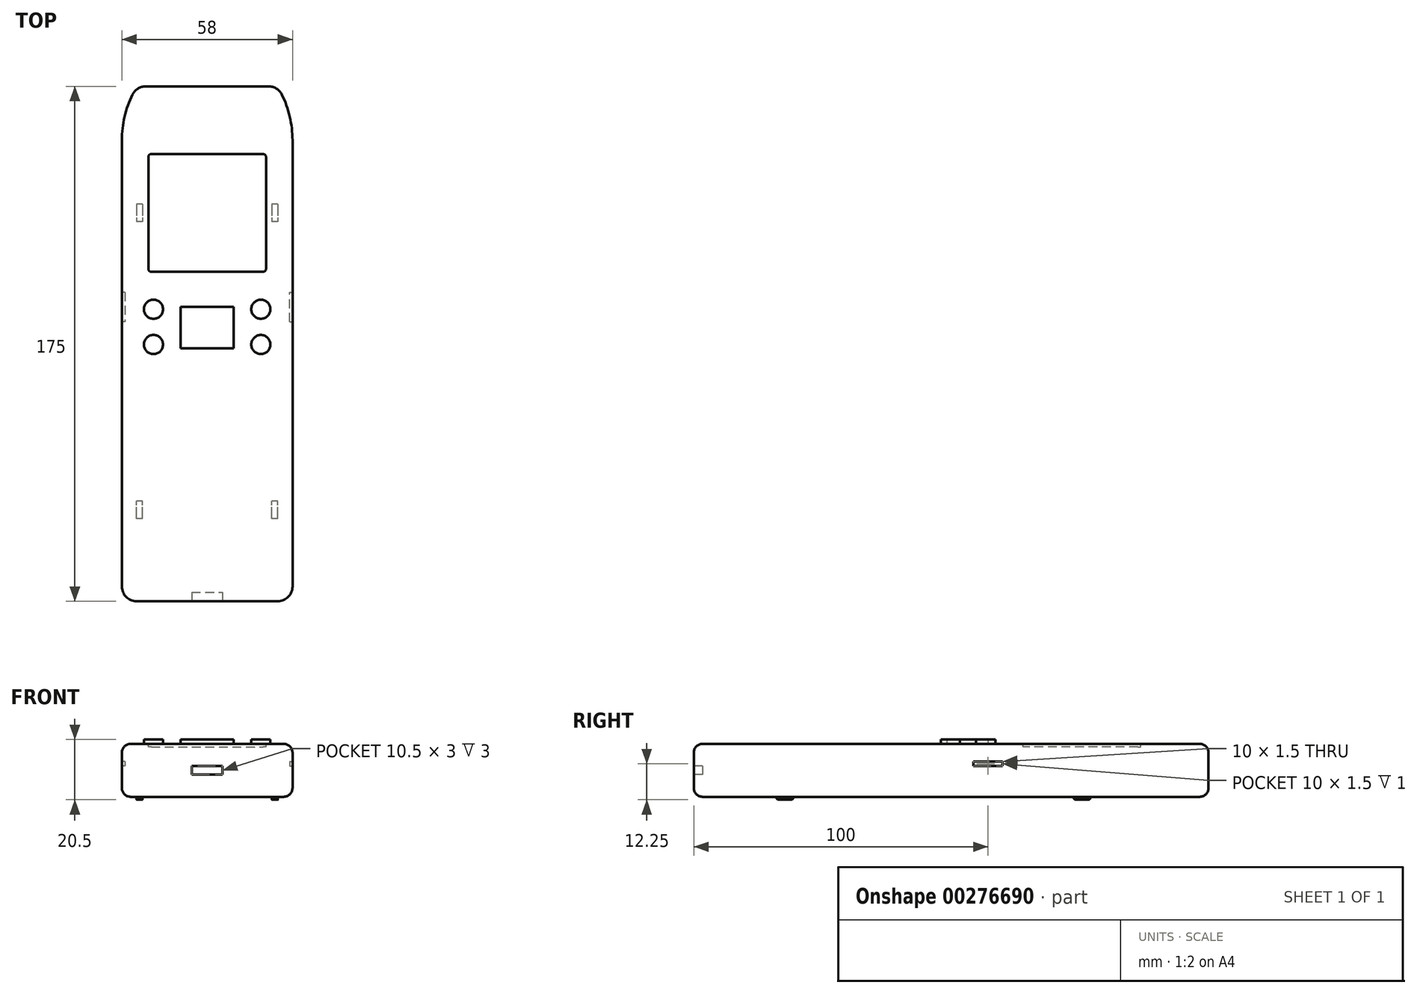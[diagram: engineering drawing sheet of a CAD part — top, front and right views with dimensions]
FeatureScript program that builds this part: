
annotation { "Feature Type Name" : "Feature", "Feature Type Description" : "" }
export const myFeature = defineFeature(function(context is Context, id is Id, definition is map)
    precondition{}
    {
        {
            var Q0;
            Q0=qCreatedBy(makeId("Top.planeOp"),FACE);
            var sketch = newSketch(context, id + "F0", { "sketchPlane" : qUnion([Q0])});
            skLineSegment(sketch, "E0.bottom", {"start": v(0, 0) * mm, "end": v(58, 0) * mm});
            skLineSegment(sketch, "E0.top", {"start": v(0, 175) * mm, "end": v(58, 175) * mm});
            skLineSegment(sketch, "E0.left", {"start": v(0, 0) * mm, "end": v(0, 175) * mm});
            skLineSegment(sketch, "E0.right", {"start": v(58, 0) * mm, "end": v(58, 175) * mm});
            skSolve(sketch);
        }
        {
            var Q0;
            Q0=makeQuery(id+"F0.imprint","IMPRINT",FACE,{"disambiguationData":[TD([[makeQuery(id+"F0.imprint","IMPRINT",EDGE,{"derivedFrom":sQuery(id+"F0.wireOp",EDGE,"E0.bottom")}),1.0]])]});
            extrude(context, id + "F1", {"entities" : qUnion([Q0]), "depth" : 18 * mm});
        }
        {
            var Q0;
            Q0=makeQuery(id+"F1.opExtrude","SWEPT_EDGE",EDGE,{"disambiguationData":[OSD([sQuery(id+"F0.wireOp",EDGE,"E0.top"),sQuery(id+"F0.wireOp",EDGE,"E0.right")])]});
            var Q1;
            Q1=makeQuery(id+"F1.opExtrude","SWEPT_EDGE",EDGE,{"disambiguationData":[OSD([sQuery(id+"F0.wireOp",EDGE,"E0.top"),sQuery(id+"F0.wireOp",EDGE,"E0.left")])]});
            chamfer(context, id + "F2", {"entities" : qUnion([Q0, Q1]), "chamferType" : ChamferType.TWO_OFFSETS, "width1" : 5 * mm, "oppositeDirection" : false, "width2" : 10 * mm, "tangentPropagation" : true});
        }
        {
            var Q0;
            Q0=makeQuery(id+"F1.opExtrude","SWEPT_EDGE",EDGE,{"disambiguationData":[OSD([sQuery(id+"F0.wireOp",EDGE,"E0.bottom"),sQuery(id+"F0.wireOp",EDGE,"E0.left")])]});
            var Q1;
            Q1=makeQuery(id+"F1.opExtrude","SWEPT_EDGE",EDGE,{"disambiguationData":[OSD([sQuery(id+"F0.wireOp",EDGE,"E0.bottom"),sQuery(id+"F0.wireOp",EDGE,"E0.right")])]});
            var Q2;
            {var subQ0=sQuery(id+"F0.wireOp",EDGE,"E0.top");Q2=makeQuery(id+"F2.opChamfer","BLEND_EDGE",EDGE,{"blendedFrom":[makeQuery(id+"F1.opExtrude","SWEPT_EDGE",EDGE,{"disambiguationData":[OSD([subQ0,sQuery(id+"F0.wireOp",EDGE,"E0.left")])]}),makeQuery(id+"F1.opExtrude","SWEPT_FACE",FACE,{"disambiguationData":[OSD([subQ0])]})],"blendedInto":[makeQuery(id+"F1.opExtrude","SWEPT_FACE",FACE,{"disambiguationData":[OSD([subQ0])]})]});}
            var Q3;
            {var subQ0=sQuery(id+"F0.wireOp",EDGE,"E0.top");Q3=makeQuery(id+"F2.opChamfer","BLEND_EDGE",EDGE,{"blendedFrom":[makeQuery(id+"F1.opExtrude","SWEPT_EDGE",EDGE,{"disambiguationData":[OSD([subQ0,sQuery(id+"F0.wireOp",EDGE,"E0.right")])]}),makeQuery(id+"F1.opExtrude","SWEPT_FACE",FACE,{"disambiguationData":[OSD([subQ0])]})],"blendedInto":[makeQuery(id+"F1.opExtrude","SWEPT_FACE",FACE,{"disambiguationData":[OSD([subQ0])]})]});}
            fillet(context, id + "F3", {"entities" : qUnion([Q0, Q1, Q2, Q3]), "radius" : 5 * mm, "tangentPropagation" : true, "allowEdgeOverflow" : false});
        }
        {
            var Q0;
            {var subQ0=sQuery(id+"F0.wireOp",EDGE,"E0.left");Q0=makeQuery(id+"F2.opChamfer","BLEND_EDGE",EDGE,{"blendedFrom":[makeQuery(id+"F1.opExtrude","SWEPT_EDGE",EDGE,{"disambiguationData":[OSD([sQuery(id+"F0.wireOp",EDGE,"E0.top"),subQ0])]}),makeQuery(id+"F1.opExtrude","SWEPT_FACE",FACE,{"disambiguationData":[OSD([subQ0])]})],"blendedInto":[makeQuery(id+"F1.opExtrude","SWEPT_FACE",FACE,{"disambiguationData":[OSD([subQ0])]})]});}
            var Q1;
            {var subQ0=sQuery(id+"F0.wireOp",EDGE,"E0.right");Q1=makeQuery(id+"F2.opChamfer","BLEND_EDGE",EDGE,{"blendedFrom":[makeQuery(id+"F1.opExtrude","SWEPT_EDGE",EDGE,{"disambiguationData":[OSD([sQuery(id+"F0.wireOp",EDGE,"E0.top"),subQ0])]}),makeQuery(id+"F1.opExtrude","SWEPT_FACE",FACE,{"disambiguationData":[OSD([subQ0])]})],"blendedInto":[makeQuery(id+"F1.opExtrude","SWEPT_FACE",FACE,{"disambiguationData":[OSD([subQ0])]})]});}
            fillet(context, id + "F4", {"entities" : qUnion([Q0, Q1]), "radius" : 35 * mm, "tangentPropagation" : true, "allowEdgeOverflow" : false});
        }
        {
            var Q0;
            Q0=makeQuery(id+"F1.opExtrude","CAP_FACE",FACE,{"disambiguationData":[OSD([sQuery(id+"F0.wireOp",EDGE,"E0.bottom"),sQuery(id+"F0.wireOp",EDGE,"E0.top"),sQuery(id+"F0.wireOp",EDGE,"E0.left"),sQuery(id+"F0.wireOp",EDGE,"E0.right")])],"isStart":false});
            var sketch = newSketch(context, id + "F5", { "sketchPlane" : qUnion([Q0])});
            skCircle(sketch, "E1", {"center": v(10.75, 99.25) * mm, "radius": 3.25 * mm});
            skCircle(sketch, "E2", {"center": v(10.75, 87.25) * mm, "radius": 3.25 * mm});
            skCircle(sketch, "E3", {"center": v(47.25, 99.25) * mm, "radius": 3.25 * mm});
            skCircle(sketch, "E4", {"center": v(47.25, 87.25) * mm, "radius": 3.25 * mm});
            skLineSegment(sketch, "E5.bottom", {"start": v(20, 100) * mm, "end": v(38, 100) * mm});
            skLineSegment(sketch, "E5.top", {"start": v(20, 86) * mm, "end": v(38, 86) * mm});
            skLineSegment(sketch, "E5.left", {"start": v(20, 100) * mm, "end": v(20, 86) * mm});
            skLineSegment(sketch, "E5.right", {"start": v(38, 100) * mm, "end": v(38, 86) * mm});
            skLineSegment(sketch, "E6.bottom", {"start": v(10, 152) * mm, "end": v(48, 152) * mm});
            skLineSegment(sketch, "E6.top", {"start": v(10, 112) * mm, "end": v(48, 112) * mm});
            skLineSegment(sketch, "E6.left", {"start": v(9, 151) * mm, "end": v(9, 113) * mm});
            skLineSegment(sketch, "E6.right", {"start": v(49, 151) * mm, "end": v(49, 113) * mm});
            skPoint(sketch, "E7.visualSharp", {"position": v(9, 152) * mm});
            skArc(sketch, "E7.filletArc", {"start": v(10, 152) * mm, "mid": v(9.3, 151.7) * mm, "end": v(9, 151) * mm});
            skPoint(sketch, "E8.visualSharp", {"position": v(49, 152) * mm});
            skArc(sketch, "E8.filletArc", {"start": v(49, 151) * mm, "mid": v(48.7, 151.7) * mm, "end": v(48, 152) * mm});
            skPoint(sketch, "E9.visualSharp", {"position": v(49, 112) * mm});
            skArc(sketch, "E9.filletArc", {"start": v(48, 112) * mm, "mid": v(48.7, 112.3) * mm, "end": v(49, 113) * mm});
            skPoint(sketch, "E10.visualSharp", {"position": v(9, 112) * mm});
            skArc(sketch, "E10.filletArc", {"start": v(9, 113) * mm, "mid": v(9.3, 112.3) * mm, "end": v(10, 112) * mm});
            skSolve(sketch);
        }
        {
            var Q0;
            Q0=makeQuery(id+"F5.imprint","IMPRINT",FACE,{"disambiguationData":[TD([[makeQuery(id+"F5.imprint","IMPRINT",EDGE,{"derivedFrom":sQuery(id+"F5.wireOp",EDGE,"E6.bottom")}),-1.0]])]});
            extrude(context, id + "F6", {"entities" : qUnion([Q0]), "operationType" : NewBodyOperationType.REMOVE, "oppositeDirection" : true, "depth" : 1 * mm});
        }
        {
            var Q0;
            Q0=makeQuery(id+"F5.imprint","IMPRINT",FACE,{"disambiguationData":[TD([[makeQuery(id+"F5.imprint","IMPRINT",EDGE,{"derivedFrom":sQuery(id+"F5.wireOp",EDGE,"E3")}),1.0]])]});
            var Q1;
            Q1=makeQuery(id+"F5.imprint","IMPRINT",FACE,{"disambiguationData":[TD([[makeQuery(id+"F5.imprint","IMPRINT",EDGE,{"derivedFrom":sQuery(id+"F5.wireOp",EDGE,"E5.bottom")}),-1.0]])]});
            var Q2;
            Q2=makeQuery(id+"F5.imprint","IMPRINT",FACE,{"disambiguationData":[TD([[makeQuery(id+"F5.imprint","IMPRINT",EDGE,{"derivedFrom":sQuery(id+"F5.wireOp",EDGE,"E1")}),1.0]])]});
            var Q3;
            Q3=makeQuery(id+"F5.imprint","IMPRINT",FACE,{"disambiguationData":[TD([[makeQuery(id+"F5.imprint","IMPRINT",EDGE,{"derivedFrom":sQuery(id+"F5.wireOp",EDGE,"E2")}),1.0]])]});
            var Q4;
            Q4=makeQuery(id+"F5.imprint","IMPRINT",FACE,{"disambiguationData":[TD([[makeQuery(id+"F5.imprint","IMPRINT",EDGE,{"derivedFrom":sQuery(id+"F5.wireOp",EDGE,"E4")}),1.0]])]});
            extrude(context, id + "F7", {"entities" : qUnion([Q0, Q1, Q2, Q3, Q4]), "operationType" : NewBodyOperationType.ADD, "depth" : 1.5 * mm});
        }
        {
            var Q0;
            Q0=makeQuery(id+"F1.opExtrude","CAP_FACE",FACE,{"disambiguationData":[OSD([sQuery(id+"F0.wireOp",EDGE,"E0.bottom"),sQuery(id+"F0.wireOp",EDGE,"E0.top"),sQuery(id+"F0.wireOp",EDGE,"E0.left"),sQuery(id+"F0.wireOp",EDGE,"E0.right")])],"isStart":true});
            var sketch = newSketch(context, id + "F8", { "sketchPlane" : qUnion([Q0])});
            skLineSegment(sketch, "E11.bottom", {"start": v(53, -28) * mm, "end": v(51, -28) * mm});
            skLineSegment(sketch, "E11.top", {"start": v(53, -34) * mm, "end": v(51, -34) * mm});
            skLineSegment(sketch, "E11.left", {"start": v(53, -28) * mm, "end": v(53, -34) * mm});
            skLineSegment(sketch, "E11.right", {"start": v(51, -28) * mm, "end": v(51, -34) * mm});
            skLineSegment(sketch, "E12.bottom", {"start": v(7, -28) * mm, "end": v(5, -28) * mm});
            skLineSegment(sketch, "E12.top", {"start": v(7, -34) * mm, "end": v(5, -34) * mm});
            skLineSegment(sketch, "E12.left", {"start": v(7, -28) * mm, "end": v(7, -34) * mm});
            skLineSegment(sketch, "E12.right", {"start": v(5, -28) * mm, "end": v(5, -34) * mm});
            skLineSegment(sketch, "E13.bottom", {"start": v(53, -135) * mm, "end": v(51, -135) * mm});
            skLineSegment(sketch, "E13.top", {"start": v(53, -129) * mm, "end": v(51, -129) * mm});
            skLineSegment(sketch, "E13.left", {"start": v(53, -135) * mm, "end": v(53, -129) * mm});
            skLineSegment(sketch, "E13.right", {"start": v(51, -135) * mm, "end": v(51, -129) * mm});
            skLineSegment(sketch, "E14.bottom", {"start": v(7, -135) * mm, "end": v(5, -135) * mm});
            skLineSegment(sketch, "E14.top", {"start": v(7, -129) * mm, "end": v(5, -129) * mm});
            skLineSegment(sketch, "E14.left", {"start": v(7, -135) * mm, "end": v(7, -129) * mm});
            skLineSegment(sketch, "E14.right", {"start": v(5, -135) * mm, "end": v(5, -129) * mm});
            skSolve(sketch);
        }
        {
            var Q0;
            Q0=makeQuery(id+"F8.imprint","IMPRINT",FACE,{"disambiguationData":[TD([[makeQuery(id+"F8.imprint","IMPRINT",EDGE,{"derivedFrom":sQuery(id+"F8.wireOp",EDGE,"E12.bottom")}),1.0]])]});
            var Q1;
            Q1=makeQuery(id+"F8.imprint","IMPRINT",FACE,{"disambiguationData":[TD([[makeQuery(id+"F8.imprint","IMPRINT",EDGE,{"derivedFrom":sQuery(id+"F8.wireOp",EDGE,"E11.bottom")}),1.0]])]});
            var Q2;
            Q2=makeQuery(id+"F8.imprint","IMPRINT",FACE,{"disambiguationData":[TD([[makeQuery(id+"F8.imprint","IMPRINT",EDGE,{"derivedFrom":sQuery(id+"F8.wireOp",EDGE,"E13.bottom")}),-1.0]])]});
            var Q3;
            Q3=makeQuery(id+"F8.imprint","IMPRINT",FACE,{"disambiguationData":[TD([[makeQuery(id+"F8.imprint","IMPRINT",EDGE,{"derivedFrom":sQuery(id+"F8.wireOp",EDGE,"E14.bottom")}),-1.0]])]});
            extrude(context, id + "F9", {"entities" : qUnion([Q0, Q1, Q2, Q3]), "operationType" : NewBodyOperationType.ADD, "depth" : 1 * mm});
        }
        {
            var Q0;
            Q0=makeQuery(id+"F1.opExtrude","CAP_EDGE",EDGE,{"disambiguationData":[OSD([sQuery(id+"F0.wireOp",EDGE,"E0.right")])],"isStart":false});
            var Q1;
            Q1=makeQuery(id+"F1.opExtrude","CAP_EDGE",EDGE,{"disambiguationData":[OSD([sQuery(id+"F0.wireOp",EDGE,"E0.right")])],"isStart":true});
            var Q2;
            Q2=makeQuery(id+"F1.opExtrude","CAP_EDGE",EDGE,{"disambiguationData":[OSD([sQuery(id+"F0.wireOp",EDGE,"E0.top")])],"isStart":false});
            var Q3;
            Q3=makeQuery(id+"F1.opExtrude","CAP_EDGE",EDGE,{"disambiguationData":[OSD([sQuery(id+"F0.wireOp",EDGE,"E0.top")])],"isStart":true});
            fillet(context, id + "F10", {"entities" : qUnion([Q0, Q1, Q2, Q3]), "radius" : 3 * mm, "tangentPropagation" : true, "allowEdgeOverflow" : false});
        }
        {
            var Q0;
            Q0=makeQuery(id+"F9.opExtrude","CAP_EDGE",EDGE,{"disambiguationData":[OSD([sQuery(id+"F8.wireOp",EDGE,"E11.top")])],"isStart":false});
            var Q1;
            Q1=makeQuery(id+"F9.opExtrude","CAP_EDGE",EDGE,{"disambiguationData":[OSD([sQuery(id+"F8.wireOp",EDGE,"E11.bottom")])],"isStart":false});
            var Q2;
            Q2=makeQuery(id+"F9.opExtrude","CAP_EDGE",EDGE,{"disambiguationData":[OSD([sQuery(id+"F8.wireOp",EDGE,"E12.bottom")])],"isStart":false});
            var Q3;
            Q3=makeQuery(id+"F9.opExtrude","CAP_EDGE",EDGE,{"disambiguationData":[OSD([sQuery(id+"F8.wireOp",EDGE,"E12.top")])],"isStart":false});
            var Q4;
            Q4=makeQuery(id+"F9.opExtrude","CAP_EDGE",EDGE,{"disambiguationData":[OSD([sQuery(id+"F8.wireOp",EDGE,"E14.top")])],"isStart":false});
            var Q5;
            Q5=makeQuery(id+"F9.opExtrude","CAP_EDGE",EDGE,{"disambiguationData":[OSD([sQuery(id+"F8.wireOp",EDGE,"E14.bottom")])],"isStart":false});
            var Q6;
            Q6=makeQuery(id+"F9.opExtrude","CAP_EDGE",EDGE,{"disambiguationData":[OSD([sQuery(id+"F8.wireOp",EDGE,"E13.top")])],"isStart":false});
            var Q7;
            Q7=makeQuery(id+"F9.opExtrude","CAP_EDGE",EDGE,{"disambiguationData":[OSD([sQuery(id+"F8.wireOp",EDGE,"E13.bottom")])],"isStart":false});
            fillet(context, id + "F11", {"entities" : qUnion([Q0, Q1, Q2, Q3, Q4, Q5, Q6, Q7]), "radius" : 1 * mm, "tangentPropagation" : true, "allowEdgeOverflow" : false});
        }
        {
            var Q0;
            Q0=makeQuery(id+"F1.opExtrude","SWEPT_FACE",FACE,{"disambiguationData":[OSD([sQuery(id+"F0.wireOp",EDGE,"E0.bottom")])]});
            var sketch = newSketch(context, id + "F12", { "sketchPlane" : qUnion([Q0])});
            skLineSegment(sketch, "E15.bottom", {"start": v(23.75, 10.5) * mm, "end": v(34.25, 10.5) * mm});
            skLineSegment(sketch, "E15.top", {"start": v(23.75, 7.5) * mm, "end": v(34.25, 7.5) * mm});
            skLineSegment(sketch, "E15.left", {"start": v(23.75, 10.5) * mm, "end": v(23.75, 7.5) * mm});
            skLineSegment(sketch, "E15.right", {"start": v(34.25, 10.5) * mm, "end": v(34.25, 7.5) * mm});
            skSolve(sketch);
        }
        {
            var Q0;
            Q0=makeQuery(id+"F12.imprint","IMPRINT",FACE,{"disambiguationData":[TD([[makeQuery(id+"F12.imprint","IMPRINT",EDGE,{"derivedFrom":sQuery(id+"F12.wireOp",EDGE,"E15.bottom")}),-1.0]])]});
            extrude(context, id + "F13", {"entities" : qUnion([Q0]), "operationType" : NewBodyOperationType.REMOVE, "oppositeDirection" : true, "depth" : 3 * mm});
        }
        {
            var Q0;
            Q0=makeQuery(id+"F1.opExtrude","SWEPT_FACE",FACE,{"disambiguationData":[OSD([sQuery(id+"F0.wireOp",EDGE,"E0.right")])]});
            var sketch = newSketch(context, id + "F14", { "sketchPlane" : qUnion([Q0])});
            skLineSegment(sketch, "E16.bottom", {"start": v(95, 12) * mm, "end": v(105, 12) * mm});
            skLineSegment(sketch, "E16.top", {"start": v(95, 10.5) * mm, "end": v(105, 10.5) * mm});
            skLineSegment(sketch, "E16.left", {"start": v(95, 12) * mm, "end": v(95, 10.5) * mm});
            skLineSegment(sketch, "E16.right", {"start": v(105, 12) * mm, "end": v(105, 10.5) * mm});
            skSolve(sketch);
        }
        {
            var Q0;
            Q0=makeQuery(id+"F14.imprint","IMPRINT",FACE,{"disambiguationData":[TD([[makeQuery(id+"F14.imprint","IMPRINT",EDGE,{"derivedFrom":sQuery(id+"F14.wireOp",EDGE,"E16.bottom")}),-1.0]])]});
            extrude(context, id + "F15", {"entities" : qUnion([Q0]), "operationType" : NewBodyOperationType.REMOVE, "oppositeDirection" : true, "depth" : 1 * mm});
        }
        {
            var Q0;
            Q0=makeQuery(id+"F1.opExtrude","SWEPT_FACE",FACE,{"disambiguationData":[OSD([sQuery(id+"F0.wireOp",EDGE,"E0.left")])]});
            var sketch = newSketch(context, id + "F16", { "sketchPlane" : qUnion([Q0])});
            skLineSegment(sketch, "E17.bottom", {"start": v(-105, 12) * mm, "end": v(-95, 12) * mm});
            skLineSegment(sketch, "E17.top", {"start": v(-105, 10.5) * mm, "end": v(-95, 10.5) * mm});
            skLineSegment(sketch, "E17.left", {"start": v(-105, 12) * mm, "end": v(-105, 10.5) * mm});
            skLineSegment(sketch, "E17.right", {"start": v(-95, 12) * mm, "end": v(-95, 10.5) * mm});
            skSolve(sketch);
        }
        {
            var Q0;
            Q0=makeQuery(id+"F16.imprint","IMPRINT",FACE,{"disambiguationData":[TD([[makeQuery(id+"F16.imprint","IMPRINT",EDGE,{"derivedFrom":sQuery(id+"F16.wireOp",EDGE,"E17.bottom")}),-1.0]])]});
            extrude(context, id + "F17", {"entities" : qUnion([Q0]), "operationType" : NewBodyOperationType.REMOVE, "oppositeDirection" : true, "depth" : 1 * mm});
        }
    });
